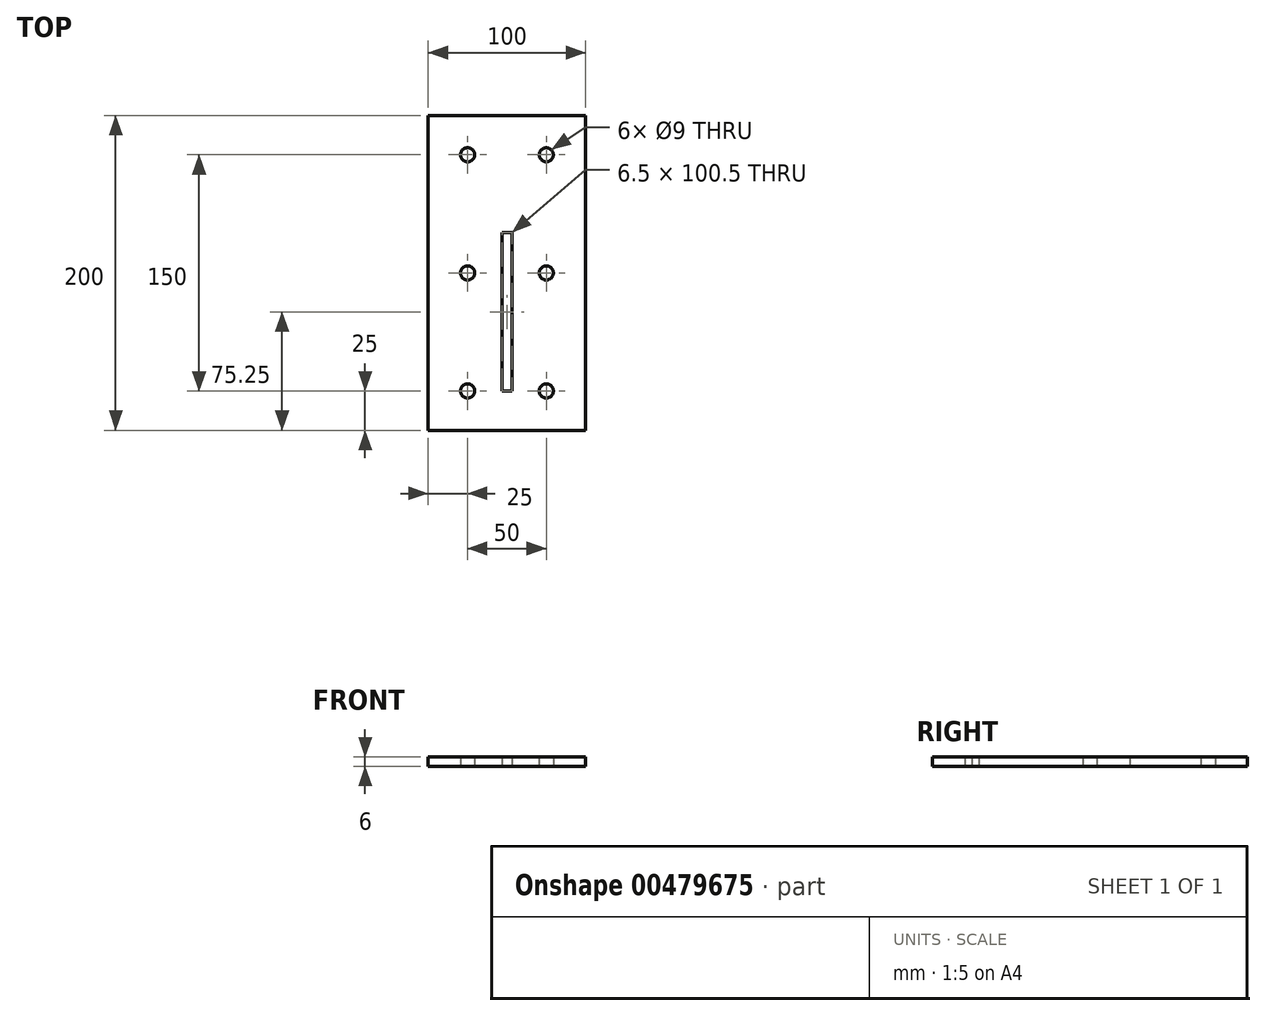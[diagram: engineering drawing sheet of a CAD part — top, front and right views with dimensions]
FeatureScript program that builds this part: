
annotation { "Feature Type Name" : "Feature", "Feature Type Description" : "" }
export const myFeature = defineFeature(function(context is Context, id is Id, definition is map)
    precondition{}
    {
        {
            var Q0;
            Q0=qCreatedBy(makeId("Top.planeOp"),FACE);
            var sketch = newSketch(context, id + "F0", { "sketchPlane" : qUnion([Q0])});
            skLineSegment(sketch, "E0.bottom", {"start": v(50, -100) * mm, "end": v(-50, -100) * mm});
            skLineSegment(sketch, "E0.top", {"start": v(50, 100) * mm, "end": v(-50, 100) * mm});
            skLineSegment(sketch, "E0.left", {"start": v(50, -100) * mm, "end": v(50, 100) * mm});
            skLineSegment(sketch, "E0.right", {"start": v(-50, -100) * mm, "end": v(-50, 100) * mm});
            skPoint(sketch, "E0.middle", {"position": v(0, 0) * mm});
            skLineSegment(sketch, "E1.bottom", {"start": v(3.25, -75) * mm, "end": v(-3.25, -75) * mm});
            skLineSegment(sketch, "E1.top", {"start": v(3.25, 25.5) * mm, "end": v(-3.25, 25.5) * mm});
            skLineSegment(sketch, "E1.left", {"start": v(3.25, -75) * mm, "end": v(3.25, 25.5) * mm});
            skLineSegment(sketch, "E1.right", {"start": v(-3.25, -75) * mm, "end": v(-3.25, 25.5) * mm});
            skPoint(sketch, "E1.middle", {"position": v(0, -24.75) * mm});
            skPoint(sketch, "E2", {"position": v(-25, 75) * mm});
            skPoint(sketch, "E3", {"position": v(25, 75) * mm});
            skPoint(sketch, "E4", {"position": v(-25, 0) * mm});
            skPoint(sketch, "E4.positionSnap0", {"position": v(-50, 0) * mm});
            skPoint(sketch, "E5", {"position": v(25, 0) * mm});
            skPoint(sketch, "E5.positionSnap0", {"position": v(50, 0) * mm});
            skPoint(sketch, "E6", {"position": v(-25, -75) * mm});
            skPoint(sketch, "E7", {"position": v(25, -75) * mm});
            skSolve(sketch);
        }
        {
            var Q0;
            Q0 = qSketchRegion(id + "F0", true);
            extrude(context, id + "F1", {"entities" : qUnion([Q0]), "depth" : 6 * mm, "offsetDistance" : 25 * mm});
        }
        {
            var Q0;
            Q0=sQuery(id+"F0.wireOp",VERTEX,"E2");
            var Q1;
            Q1=sQuery(id+"F0.wireOp",VERTEX,"E3");
            var Q2;
            Q2=sQuery(id+"F0.wireOp",VERTEX,"E4");
            var Q3;
            Q3=sQuery(id+"F0.wireOp",VERTEX,"E5");
            var Q4;
            Q4=sQuery(id+"F0.wireOp",VERTEX,"E7");
            var Q5;
            Q5=sQuery(id+"F0.wireOp",VERTEX,"E6");
            var Q6;
            Q6=makeQuery(id+"F1.opExtrude","SWEPT_BODY",BODY,{"disambiguationData":[OSD([sQuery(id+"F0.wireOp",EDGE,"E0.bottom"),sQuery(id+"F0.wireOp",EDGE,"E0.top"),sQuery(id+"F0.wireOp",EDGE,"E0.left"),sQuery(id+"F0.wireOp",EDGE,"E0.right"),sQuery(id+"F0.wireOp",EDGE,"E1.bottom"),sQuery(id+"F0.wireOp",EDGE,"E1.top"),sQuery(id+"F0.wireOp",EDGE,"E1.left"),sQuery(id+"F0.wireOp",EDGE,"E1.right")])]});
            hole(context, id + "F2", {"style" : HoleStyle.SIMPLE, "endStyle" : HoleEndStyle.THROUGH, "oppositeDirection" : true, "holeDiameter" : 9 * mm, "majorDiameter" : 5 * mm, "isTappedThrough" : true, "tappedDepth" : 12 * mm, "tapClearance" : 3, "locations" : qUnion([Q0, Q1, Q2, Q3, Q4, Q5]), "scope" : qUnion([Q6])});
        }
    });
